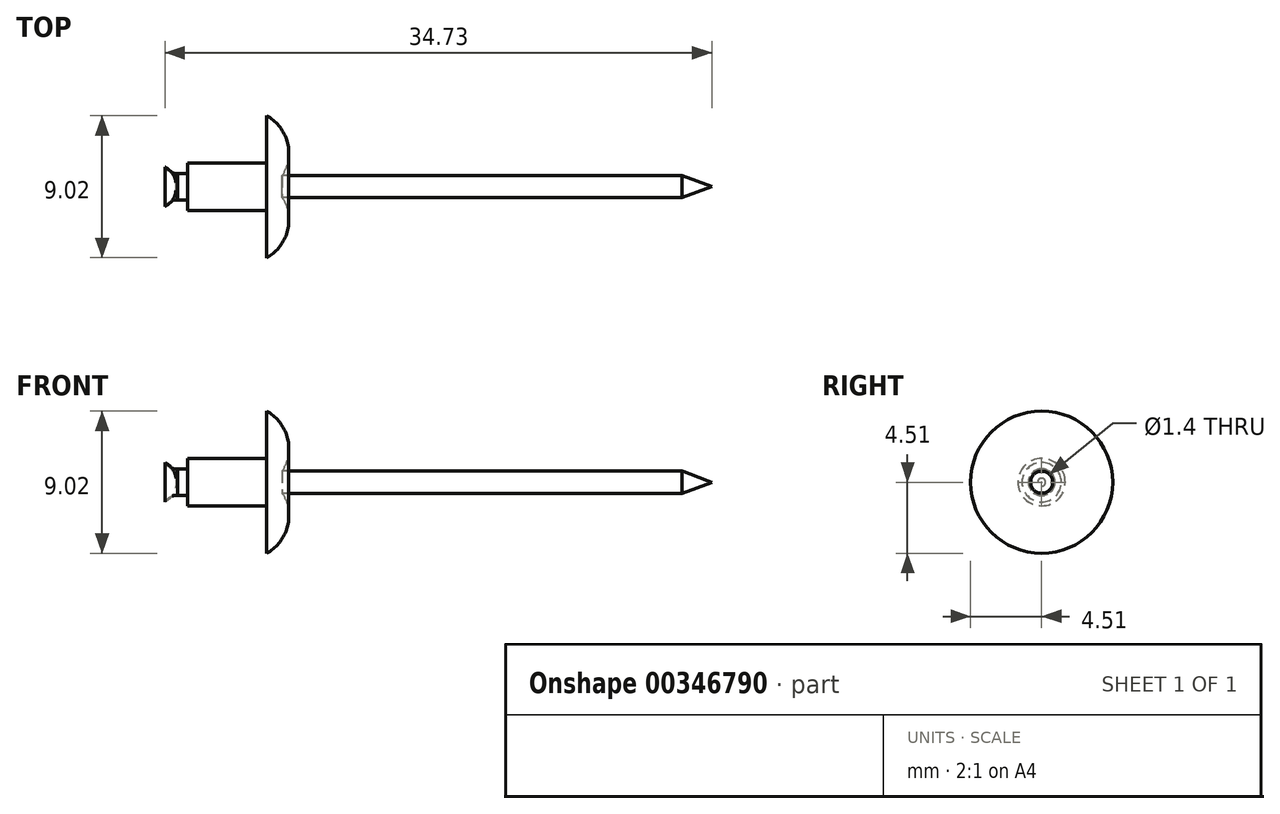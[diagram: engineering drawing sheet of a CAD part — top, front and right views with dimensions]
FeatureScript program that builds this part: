
annotation { "Feature Type Name" : "Feature", "Feature Type Description" : "" }
export const myFeature = defineFeature(function(context is Context, id is Id, definition is map)
    precondition{}
    {
        {
            var Q0;
            Q0=qCreatedBy(makeId("Front.planeOp"),FACE);
            var sketch = newSketch(context, id + "F0", { "sketchPlane" : qUnion([Q0])});
            skArc(sketch, "E0", {"start": v(1.8, 1.25) * mm, "mid": v(0.53, 1.15) * mm, "end": v(0, 0) * mm});
            skPoint(sketch, "E1", {"position": v(2.6, 0.85) * mm});
            skArc(sketch, "E2", {"start": v(1.8, 1.25) * mm, "mid": v(2.13, 0.93) * mm, "end": v(2.6, 0.85) * mm});
            skLineSegment(sketch, "E3", {"start": v(2.6, 0.85) * mm, "end": v(3.24, 0.85) * mm});
            skLineSegment(sketch, "E4", {"start": v(3.24, 0.85) * mm, "end": v(3.24, 1.5) * mm});
            skPoint(sketch, "E5", {"position": v(8.24, 1.5) * mm});
            skLineSegment(sketch, "E6", {"start": v(3.24, 1.5) * mm, "end": v(8.24, 1.5) * mm});
            skLineSegment(sketch, "E7", {"start": v(8.24, 1.5) * mm, "end": v(8.24, 4.5) * mm});
            skArc(sketch, "E8", {"start": v(9.24, 0.7) * mm, "mid": v(9.56, 2.83) * mm, "end": v(8.23, 4.51) * mm});
            skLineSegment(sketch, "E9", {"start": v(9.24, 0.7) * mm, "end": v(34.64, 0.7) * mm});
            skLineSegment(sketch, "E10", {"start": v(34.64, 0.7) * mm, "end": v(36.52, 0) * mm});
            skSolve(sketch);
        }
        {
            var Q0;
            Q0=qCreatedBy(makeId("Front.planeOp"),FACE);
            var sketch = newSketch(context, id + "F1", { "sketchPlane" : qUnion([Q0])});
            skLineSegment(sketch, "E11", {"start": v(-18.75, 0) * mm, "end": v(-40.84, 0) * mm});
            skSolve(sketch);
        }
        {
            var Q0;
            Q0 = qConstructionFilter(qBodyType(qCreatedBy(id + "F0" ,EDGE), BodyType.WIRE), ConstructionObject.NO);
            var Q1;
            Q1=sQuery(id+"F1.wireOp",EDGE,"E11");
            revolve(context, id + "F2", {"bodyType" : ToolBodyType.SURFACE, "surfaceEntities" : qUnion([Q0]), "axis" : qUnion([Q1]), "revolveType" : RevolveType.FULL});
        }
    });
